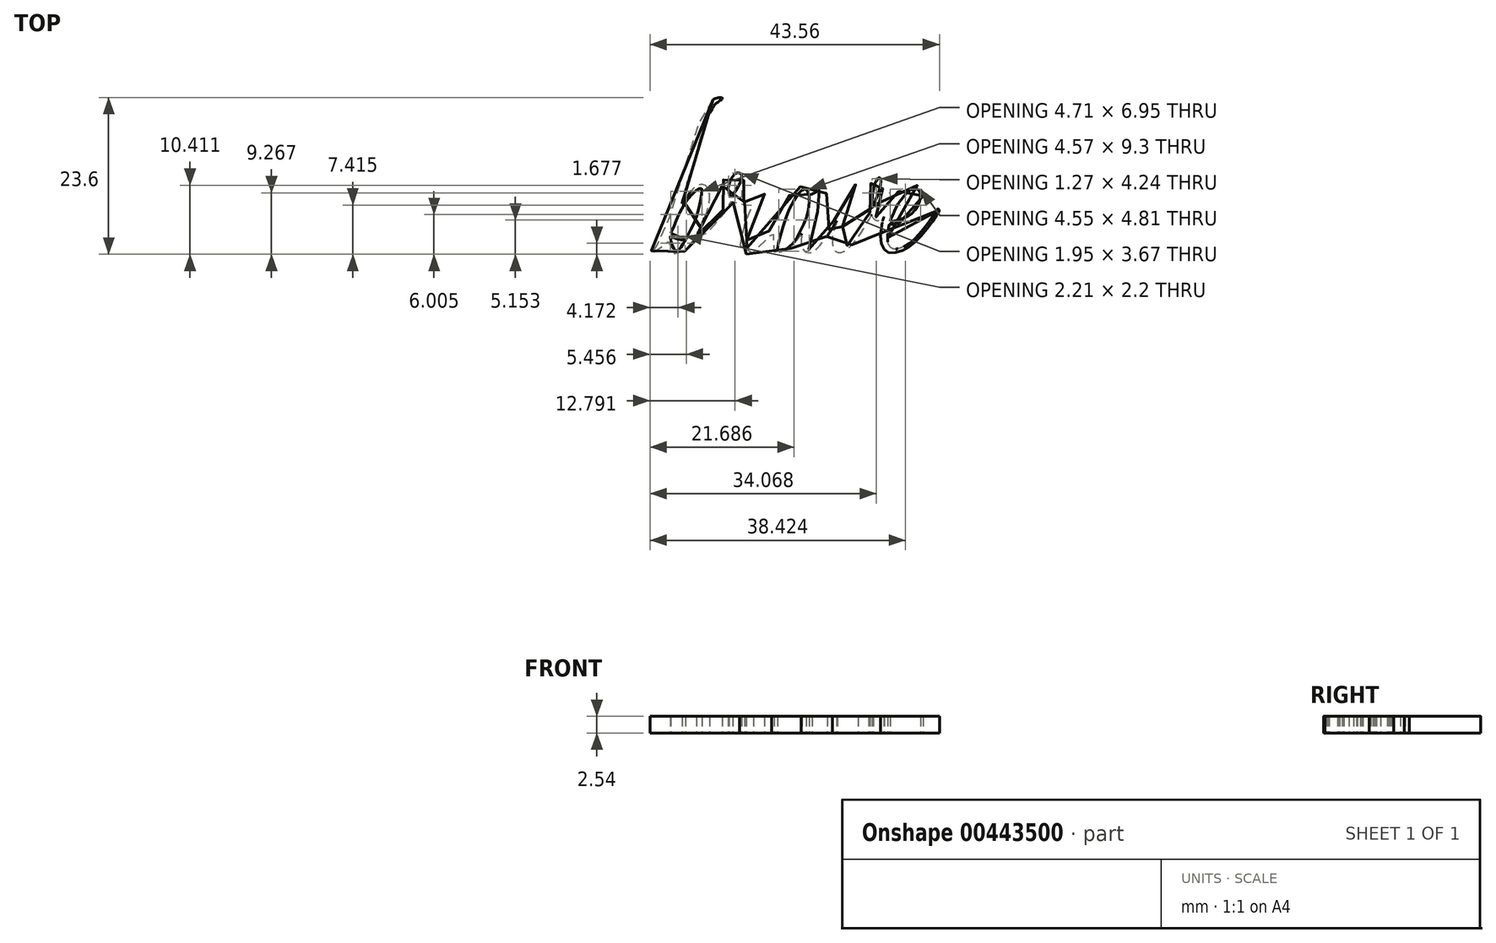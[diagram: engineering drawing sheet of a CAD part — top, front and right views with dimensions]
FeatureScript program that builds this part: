
annotation { "Feature Type Name" : "Feature", "Feature Type Description" : "" }
export const myFeature = defineFeature(function(context is Context, id is Id, definition is map)
    precondition{}
    {
        {
            var Q0;
            Q0=qCreatedBy(makeId("Top.planeOp"),FACE);
            var sketch = newSketch(context, id + "F0", { "sketchPlane" : qUnion([Q0])});
            skPoint(sketch, "E0.middle", {"position": v(0, 0) * mm});
            skFitSpline(sketch, "E1", {"points": [v(-15.92, -8.34) * mm, v(-15.17, -8.7) * mm, v(-14.11, -9.02) * mm, v(-13.49, -9.15) * mm, v(-13.43, -8.96) * mm, v(-12.61, -7.28) * mm, v(-11.74, -4.9) * mm, v(-11.24, -2.3) * mm, v(-11.24, -1.67) * mm, v(-11.62, -1.67) * mm, v(-12.55, -2.35) * mm, v(-13.74, -3.85) * mm, v(-14.48, -5.16) * mm, v(-15.23, -6.9) * mm, v(-15.73, -8.02) * mm, v(-15.92, -8.34) * mm]});
            skFitSpline(sketch, "E2", {"points": [v(-15.95, -8.78) * mm, v(-15.35, -9.07) * mm, v(-14.52, -9.35) * mm, v(-13.7, -9.44) * mm, v(-13.67, -9.44) * mm, v(-13.9, -9.75) * mm, v(-14.4, -10.5) * mm, v(-14.95, -10.98) * mm, v(-15.27, -10.9) * mm, v(-15.67, -10.21) * mm, v(-15.9, -9.33) * mm, v(-15.95, -8.78) * mm]});
            skFitSpline(sketch, "E3", {"points": [v(-6.79, -2.98) * mm, v(-6.37, -2.35) * mm, v(-5.5, -0.87) * mm, v(-5.22, 0.21) * mm, v(-5.33, 0.56) * mm, v(-5.8, 0.72) * mm, v(-6.24, 0.54) * mm, v(-6.7, 0) * mm, v(-7.03, -0.67) * mm, v(-7.23, -1.5) * mm, v(-7.14, -2.24) * mm, v(-6.79, -2.98) * mm]});
            skFitSpline(sketch, "E4", {"points": [v(2.73, -3.32) * mm, v(3.6, -2.07) * mm, v(4.12, -1.78) * mm, v(4.41, -1.78) * mm, v(4.8, -2.36) * mm, v(4.94, -3.85) * mm, v(4.5, -6.06) * mm, v(3.55, -8.17) * mm, v(2.54, -9.8) * mm, v(1.58, -10.72) * mm, v(0.61, -11.1) * mm, v(0.23, -10.86) * mm, v(0.33, -9.85) * mm, v(1.14, -6.87) * mm, v(2.15, -4.37) * mm, v(2.73, -3.32) * mm]});
            skFitSpline(sketch, "E5", {"points": [v(15.21, -0.17) * mm, v(14.96, -0.63) * mm, v(14.76, -1.2) * mm, v(14.59, -1.9) * mm, v(14.47, -2.69) * mm, v(14.42, -3.27) * mm, v(14.42, -3.8) * mm, v(14.42, -4.3) * mm, v(14.44, -4.45) * mm, v(14.47, -4.44) * mm, v(14.64, -4.1) * mm, v(15.12, -2.93) * mm, v(15.5, -1.75) * mm, v(15.69, -0.82) * mm, v(15.69, -0.2) * mm, v(15.6, -0.04) * mm, v(15.56, 0) * mm, v(15.38, -0.04) * mm, v(15.21, -0.17) * mm]});
            skFitSpline(sketch, "E6", {"points": [v(17.13, -6.55) * mm, v(18.13, -6.44) * mm, v(19.68, -5.88) * mm, v(20.9, -4.8) * mm, v(21.65, -3.21) * mm, v(21.65, -2.33) * mm, v(21.32, -1.77) * mm, v(20.87, -1.7) * mm, v(20.13, -1.88) * mm, v(19.31, -2.66) * mm, v(18.35, -3.92) * mm, v(17.8, -4.92) * mm, v(17.42, -5.84) * mm, v(17.13, -6.55) * mm]});
            skPoint(sketch, "E7.54.internal.snap0", {"position": v(-5.23, 11.71) * mm});
            skFitSpline(sketch, "E7", {"points": [v(-9.54, 11.71) * mm, v(-10.79, 10.08) * mm, v(-11.84, 7.77) * mm, v(-14.46, -0.67) * mm, v(-16.43, -6.95) * mm, v(-17.2, -8.73) * mm, v(-18.56, -10.85) * mm, v(-18.98, -11.17) * mm, v(-19.02, -11.25) * mm, v(-19, -11.32) * mm, v(-18.84, -11.37) * mm, v(-18.48, -11.36) * mm, v(-17.92, -11.12) * mm, v(-17.51, -10.8) * mm, v(-16.95, -10.18) * mm, v(-16.62, -9.7) * mm, v(-16.41, -9.31) * mm, v(-16.37, -9.24) * mm, v(-16.33, -9.25) * mm, v(-16.27, -9.54) * mm, v(-16.11, -10.2) * mm, v(-15.9, -10.74) * mm, v(-15.63, -11.2) * mm, v(-15.18, -11.53) * mm, v(-14.92, -11.55) * mm, v(-14.46, -11.49) * mm, v(-13.8, -11.08) * mm, v(-13.31, -10.71) * mm, v(-12.72, -9.94) * mm, v(-12.37, -9.35) * mm, v(-12.36, -9.3) * mm, v(-12.32, -9.28) * mm, v(-12.1, -9.26) * mm, v(-11.79, -9.1) * mm, v(-10.93, -8.65) * mm, v(-9.49, -7.45) * mm, v(-8.24, -5.86) * mm, v(-7.52, -4.85) * mm, v(-7.23, -4.32) * mm, v(-6.93, -3.8) * mm, v(-6.8, -3.6) * mm, v(-6.7, -3.64) * mm, v(-6.29, -3.88) * mm, v(-5.4, -4.12) * mm, v(-4.48, -4.08) * mm, v(-3.82, -3.88) * mm, v(-3.51, -3.73) * mm, v(-3.46, -3.7) * mm, v(-3.48, -3.82) * mm, v(-3.84, -4.63) * mm, v(-4.21, -5.46) * mm, v(-4.64, -6.55) * mm, v(-5.43, -8.71) * mm, v(-5.54, -9.86) * mm, v(-5.23, -11.1) * mm, v(-4.54, -11.5) * mm, v(-3.39, -11.3) * mm, v(-1.83, -9.86) * mm, v(-0.83, -8.53) * mm, v(-0.43, -7.79) * mm, v(-0.35, -7.73) * mm, v(-0.33, -7.8) * mm, v(-0.43, -8.32) * mm, v(-0.69, -9.28) * mm, v(-0.69, -10.28) * mm, v(-0.28, -11.25) * mm, v(0.31, -11.5) * mm, v(1.46, -11.1) * mm, v(2.35, -10.58) * mm, v(3.2, -9.5) * mm, v(3.68, -8.7) * mm, v(3.78, -8.52) * mm, v(3.8, -8.5) * mm, v(3.83, -8.54) * mm, v(3.76, -8.9) * mm, v(3.72, -9.52) * mm, v(3.72, -10) * mm, v(3.89, -10.56) * mm, v(4.05, -10.9) * mm, v(4.37, -11.2) * mm, v(4.92, -11.33) * mm, v(5.34, -11.23) * mm, v(6.07, -10.69) * mm, v(6.52, -10.23) * mm, v(7.33, -9.2) * mm, v(8, -8.27) * mm, v(8.5, -7.5) * mm, v(8.9, -6.75) * mm, v(9, -6.57) * mm, v(9.05, -6.58) * mm, v(9.03, -6.78) * mm, v(8.74, -7.64) * mm, v(8.47, -8.61) * mm, v(8.4, -9.39) * mm, v(8.4, -9.82) * mm, v(8.64, -10.75) * mm, v(9.2, -11.26) * mm, v(9.85, -11.23) * mm, v(10.58, -10.84) * mm, v(11.29, -10.2) * mm, v(12.04, -9.32) * mm, v(12.83, -8.13) * mm, v(13.9, -6.37) * mm, v(14.26, -5.7) * mm, v(14.29, -5.63) * mm, v(14.33, -5.67) * mm, v(14.42, -5.9) * mm, v(14.72, -6.27) * mm, v(15.2, -6.48) * mm, v(15.69, -6.34) * mm, v(16.12, -5.94) * mm, v(16.14, -5.9) * mm, v(16.19, -5.91) * mm, v(16.17, -5.97) * mm, v(16.12, -6.08) * mm, v(15.98, -6.57) * mm, v(15.8, -7.41) * mm, v(15.69, -8.87) * mm, v(15.88, -10.18) * mm, v(16.48, -11.1) * mm, v(17.22, -11.36) * mm, v(18.57, -11.1) * mm, v(19.7, -10.61) * mm, v(20.74, -9.81) * mm, v(22.34, -8.16) * mm, v(23.5, -6.58) * mm, v(24.17, -5.54) * mm, v(24.54, -4.95) * mm, v(24.41, -4.7) * mm, v(24.23, -4.7) * mm, v(24.06, -4.97) * mm, v(23.68, -5.59) * mm, v(23, -6.62) * mm, v(22.1, -7.81) * mm, v(21.28, -8.74) * mm, v(20.5, -9.51) * mm, v(19.53, -10.22) * mm, v(18.52, -10.64) * mm, v(17.48, -10.7) * mm, v(16.86, -9.98) * mm, v(16.73, -9.1) * mm, v(16.86, -7.64) * mm, v(16.97, -7.07) * mm, v(17.02, -7.02) * mm, v(17.1, -7.02) * mm, v(17.56, -7.02) * mm, v(18.28, -6.9) * mm, v(19.08, -6.62) * mm, v(20.1, -6.1) * mm, v(21.13, -5.15) * mm, v(21.79, -4.1) * mm, v(22.07, -3.21) * mm, v(22.07, -2.33) * mm, v(21.84, -1.58) * mm, v(21.1, -1.15) * mm, v(20.44, -1.04) * mm, v(19.59, -1.27) * mm, v(18.67, -1.84) * mm, v(17.67, -2.9) * mm, v(16.87, -4.18) * mm, v(16.44, -4.92) * mm, v(15.93, -5.61) * mm, v(15.41, -6.01) * mm, v(14.93, -5.92) * mm, v(14.61, -5.32) * mm, v(14.6, -5.18) * mm, v(14.6, -5.06) * mm, v(14.7, -4.8) * mm, v(14.99, -4.24) * mm, v(15.5, -3.07) * mm, v(15.93, -1.88) * mm, v(16.24, -0.54) * mm, v(16.15, 0.25) * mm, v(15.69, 0.56) * mm, v(15.1, 0.45) * mm, v(14.7, 0.1) * mm, v(14.35, -0.52) * mm, v(14.08, -1.27) * mm, v(13.93, -2.36) * mm, v(13.9, -3.36) * mm, v(13.93, -4.2) * mm, v(14, -4.66) * mm, v(14.09, -4.97) * mm, v(14.1, -5.16) * mm, v(14.06, -5.28) * mm, v(13.75, -5.88) * mm, v(12.88, -7.43) * mm, v(12.2, -8.42) * mm, v(11.48, -9.39) * mm, v(10.52, -10.35) * mm, v(9.85, -10.73) * mm, v(9.51, -10.73) * mm, v(9.22, -10.5) * mm, v(9.32, -9.72) * mm, v(9.51, -8.81) * mm, v(9.85, -7.61) * mm, v(10.71, -5.4) * mm, v(11.62, -3.24) * mm, v(12.3, -1.75) * mm, v(12.25, -1.41) * mm, v(11.91, -1.08) * mm, v(11.48, -1.17) * mm, v(11, -2.04) * mm, v(10.28, -3.57) * mm, v(9.6, -4.8) * mm, v(8.43, -6.92) * mm, v(7.4, -8.55) * mm, v(6.77, -9.36) * mm, v(5.91, -10.3) * mm, v(5.2, -10.84) * mm, v(4.97, -10.84) * mm, v(4.57, -10.7) * mm, v(4.51, -10.07) * mm, v(4.8, -8.9) * mm, v(5.37, -7.16) * mm, v(6.02, -5.56) * mm, v(7, -3.36) * mm, v(7.64, -2.1) * mm, v(7.6, -1.75) * mm, v(7.38, -1.5) * mm, v(6.92, -1.42) * mm, v(6.67, -1.62) * mm, v(6.4, -2.05) * mm, v(6.04, -2.77) * mm, v(5.75, -3.4) * mm, v(5.55, -3.85) * mm, v(5.46, -4.03) * mm, v(5.42, -4.03) * mm, v(5.4, -3.95) * mm, v(5.4, -3.61) * mm, v(5.36, -2.9) * mm, v(5.2, -2.17) * mm, v(4.71, -1.5) * mm, v(4.42, -1.32) * mm, v(4.02, -1.29) * mm, v(3.42, -1.42) * mm, v(2.74, -1.81) * mm, v(2.08, -2.48) * mm, v(1.37, -3.61) * mm, v(0.61, -4.8) * mm, v(0.23, -5.49) * mm, v(-0.45, -6.83) * mm, v(-1.07, -8.02) * mm, v(-1.99, -9.33) * mm, v(-3.04, -10.39) * mm, v(-3.96, -10.86) * mm, v(-4.44, -10.53) * mm, v(-4.53, -9.8) * mm, v(-4.1, -8.02) * mm, v(-2.95, -5.4) * mm, v(-2.08, -3.32) * mm, v(-1.8, -2.65) * mm, v(-1.8, -2.36) * mm, v(-2, -2.02) * mm, v(-2.44, -1.99) * mm, v(-2.84, -2.36) * mm, v(-3.03, -2.88) * mm, v(-3.58, -3.32) * mm, v(-4.36, -3.7) * mm, v(-5.1, -3.7) * mm, v(-5.77, -3.58) * mm, v(-6.33, -3.32) * mm, v(-6.55, -3.14) * mm, v(-6.51, -3.1) * mm, v(-6.41, -3) * mm, v(-5.8, -2.05) * mm, v(-4.9, -0.46) * mm, v(-4.9, 0.64) * mm, v(-5.61, 1.27) * mm, v(-6.53, 1.27) * mm, v(-7.4, 0.79) * mm, v(-7.82, 0.21) * mm, v(-8.06, -0.67) * mm, v(-8.16, -1.67) * mm, v(-7.78, -2.67) * mm, v(-7.25, -3.32) * mm, v(-7.15, -3.4) * mm, v(-7.15, -3.43) * mm, v(-7.6, -4.24) * mm, v(-8.39, -5.43) * mm, v(-9.16, -6.44) * mm, v(-10.02, -7.43) * mm, v(-10.65, -8.02) * mm, v(-11.53, -8.54) * mm, v(-12.02, -8.76) * mm, v(-12, -8.7) * mm, v(-11.93, -8.55) * mm, v(-11.55, -7.84) * mm, v(-10.88, -6.25) * mm, v(-10.22, -4.25) * mm, v(-10.1, -2.35) * mm, v(-10.55, -1.32) * mm, v(-11.24, -1.06) * mm, v(-12.03, -1.32) * mm, v(-12.89, -2.1) * mm, v(-13.43, -2.95) * mm, v(-13.5, -3.04) * mm, v(-13.7, -3.32) * mm, v(-13.97, -3.72) * mm, v(-14.13, -3.92) * mm, v(-14.18, -3.85) * mm, v(-14.13, -3.6) * mm, v(-13, 0.21) * mm, v(-12.11, 3.35) * mm, v(-11.24, 6.58) * mm, v(-10.1, 9.49) * mm, v(-9.12, 11.1) * mm, v(-8.66, 11.46) * mm, v(-8.13, 11.94) * mm, v(-8.46, 12.04) * mm, v(-9.54, 11.71) * mm]});
            skSolve(sketch);
        }
        {
            var Q0;
            Q0 = qSketchRegion(id + "F0", true);
            extrude(context, id + "F1", {"entities" : qUnion([Q0]), "depth" : 2.54 * mm});
        }
    });
